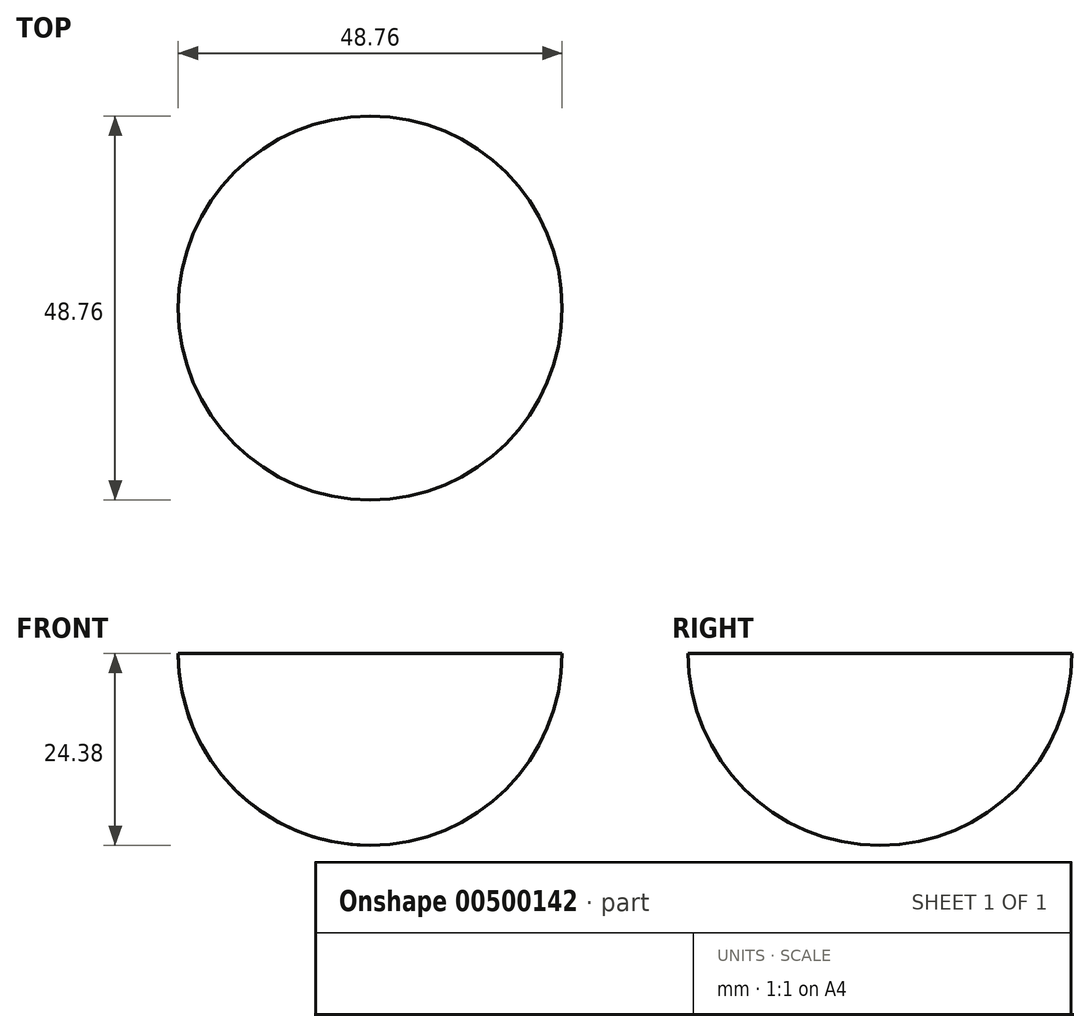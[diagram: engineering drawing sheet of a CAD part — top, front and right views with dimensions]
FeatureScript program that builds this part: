
annotation { "Feature Type Name" : "Feature", "Feature Type Description" : "" }
export const myFeature = defineFeature(function(context is Context, id is Id, definition is map)
    precondition{}
    {
        {
            var Q0;
            Q0=qCreatedBy(makeId("Front.planeOp"),FACE);
            var sketch = newSketch(context, id + "F0", { "sketchPlane" : qUnion([Q0])});
            skArc(sketch, "E0", {"start": v(0, -24.38) * mm, "mid": v(-17.24, -17.24) * mm, "end": v(-24.38, 0) * mm});
            skSolve(sketch);
        }
        {
            var Q0;
            Q0=qCreatedBy(makeId("Front.planeOp"),FACE);
            var sketch = newSketch(context, id + "F1", { "sketchPlane" : qUnion([Q0])});
            skLineSegment(sketch, "E1", {"start": v(0, 0) * mm, "end": v(0, -35.1) * mm});
            skSolve(sketch);
        }
        {
            var Q0;
            Q0=sQuery(id+"F0.wireOp",EDGE,"E0");
            var Q1;
            Q1=sQuery(id+"F1.wireOp",EDGE,"E1");
            revolve(context, id + "F2", {"bodyType" : ToolBodyType.SURFACE, "surfaceEntities" : qUnion([Q0]), "axis" : qUnion([Q1]), "revolveType" : RevolveType.FULL});
        }
    });
